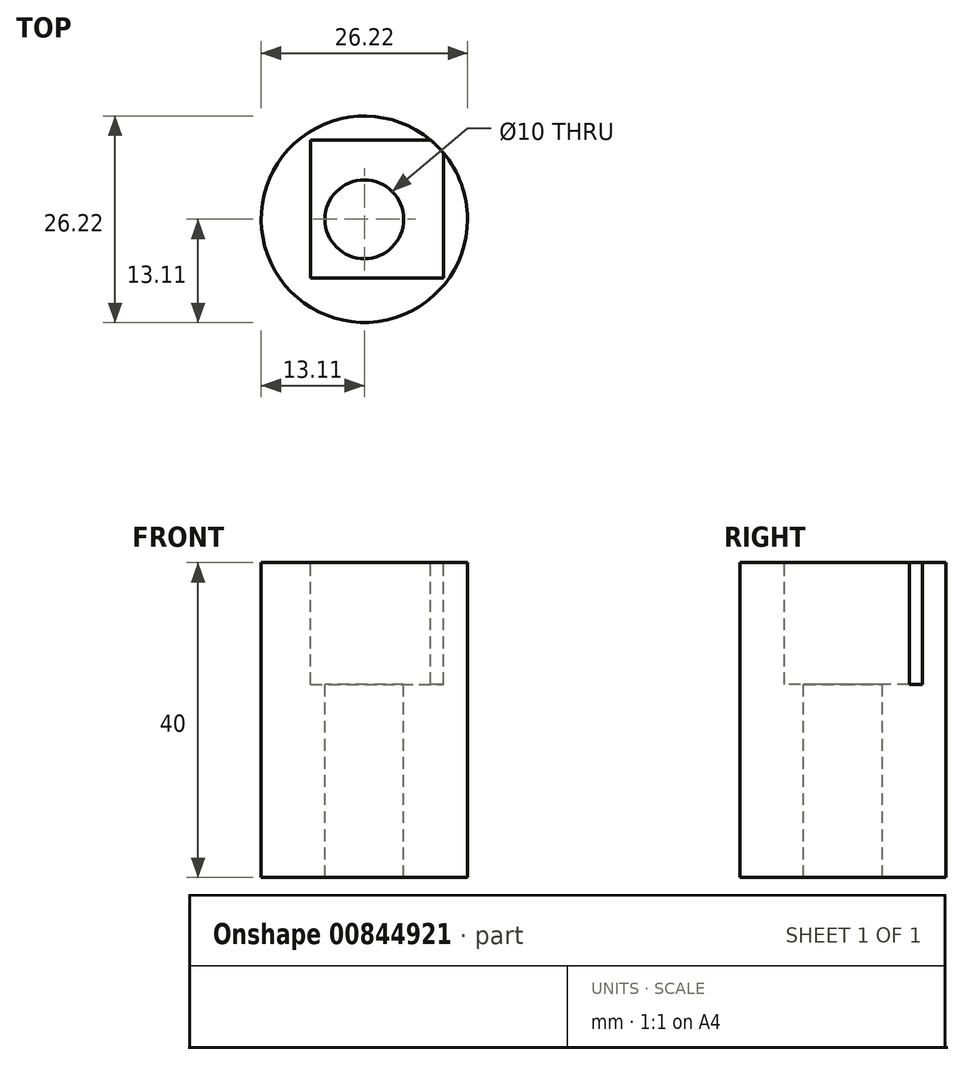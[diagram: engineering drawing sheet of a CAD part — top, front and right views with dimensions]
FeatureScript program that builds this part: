
annotation { "Feature Type Name" : "Feature", "Feature Type Description" : "" }
export const myFeature = defineFeature(function(context is Context, id is Id, definition is map)
    precondition{}
    {
        {
            var Q0;
            Q0=qCreatedBy(makeId("Top.planeOp"),FACE);
            var sketch = newSketch(context, id + "F0", { "sketchPlane" : qUnion([Q0])});
            skCircle(sketch, "E0", {"center": v(0, 0) * mm, "radius": 13.12 * mm, "construction": true});
            skSolve(sketch);
        }
        {
            var Q0;
            Q0=qCreatedBy(makeId("Top.planeOp"),FACE);
            var sketch = newSketch(context, id + "F1", { "sketchPlane" : qUnion([Q0])});
            skCircle(sketch, "E1", {"center": v(0, 0) * mm, "radius": 13.1 * mm});
            skCircle(sketch, "E2", {"center": v(0, 0) * mm, "radius": 5 * mm});
            skCircle(sketch, "E3.0", {"center": v(0, 0) * mm, "radius": 13.12 * mm});
            skSolve(sketch);
        }
        {
            var Q0;
            Q0=makeQuery(id+"F1.imprint","IMPRINT",FACE,{"disambiguationData":[TD([[makeQuery(id+"F1.imprint","IMPRINT",EDGE,{"derivedFrom":sQuery(id+"F1.wireOp",EDGE,"E1")}),1.0]])]});
            extrude(context, id + "F2", {"entities" : qUnion([Q0]), "oppositeDirection" : true, "depth" : 25 * mm, "offsetDistance" : 25 * mm, "hasSecondDirection" : true, "secondDirectionOppositeDirection" : false, "secondDirectionDepth" : 15 * mm});
        }
        {
            var Q0;
            Q0=qCreatedBy(makeId("Top.planeOp"),FACE);
            cPlane(context, id + "F3", {"entities" : qUnion([Q0]), "cplaneType" : CPlaneType.OFFSET, "offset" : 15 * mm, "width" : 150 * mm, "height" : 150 * mm});
        }
        {
            var Q0;
            Q0=qCreatedBy(id+"F3.planeOp",FACE);
            var sketch = newSketch(context, id + "F4", { "sketchPlane" : qUnion([Q0])});
            skPoint(sketch, "E4.0", {"position": v(1.6, 1.3) * mm});
            skLineSegment(sketch, "E5.bottom", {"start": v(-6.85, 10.06) * mm, "end": v(10.04, 10.06) * mm});
            skLineSegment(sketch, "E5.top", {"start": v(-6.85, -7.46) * mm, "end": v(10.04, -7.46) * mm});
            skLineSegment(sketch, "E5.left", {"start": v(-6.85, 10.06) * mm, "end": v(-6.85, -7.46) * mm});
            skLineSegment(sketch, "E5.right", {"start": v(10.04, 10.06) * mm, "end": v(10.04, -7.46) * mm});
            skLineSegment(sketch, "E6.bottom", {"start": v(-6.85, -7.46) * mm, "end": v(-10.87, -7.46) * mm});
            skLineSegment(sketch, "E6.top", {"start": v(-6.85, -5.84) * mm, "end": v(-10.87, -5.84) * mm});
            skLineSegment(sketch, "E6.left", {"start": v(-6.85, -7.46) * mm, "end": v(-6.85, -5.84) * mm});
            skLineSegment(sketch, "E6.right", {"start": v(-10.87, -7.46) * mm, "end": v(-10.87, -5.84) * mm});
            skSolve(sketch);
        }
        {
            var Q0;
            {var subQ3=sQuery(id+"F4.wireOp",EDGE,"E5.bottom");Q0=makeQuery(id+"F4.imprint","IMPRINT",FACE,{"disambiguationData":[TD([[makeQuery(id+"F4.imprint","IMPRINT",EDGE,{"derivedFrom":subQ3}),-1.0]])]});}
            extrude(context, id + "F5", {"entities" : qUnion([Q0]), "operationType" : NewBodyOperationType.REMOVE, "oppositeDirection" : true, "depth" : 15.48 * mm, "offsetDistance" : 25 * mm});
        }
    });
